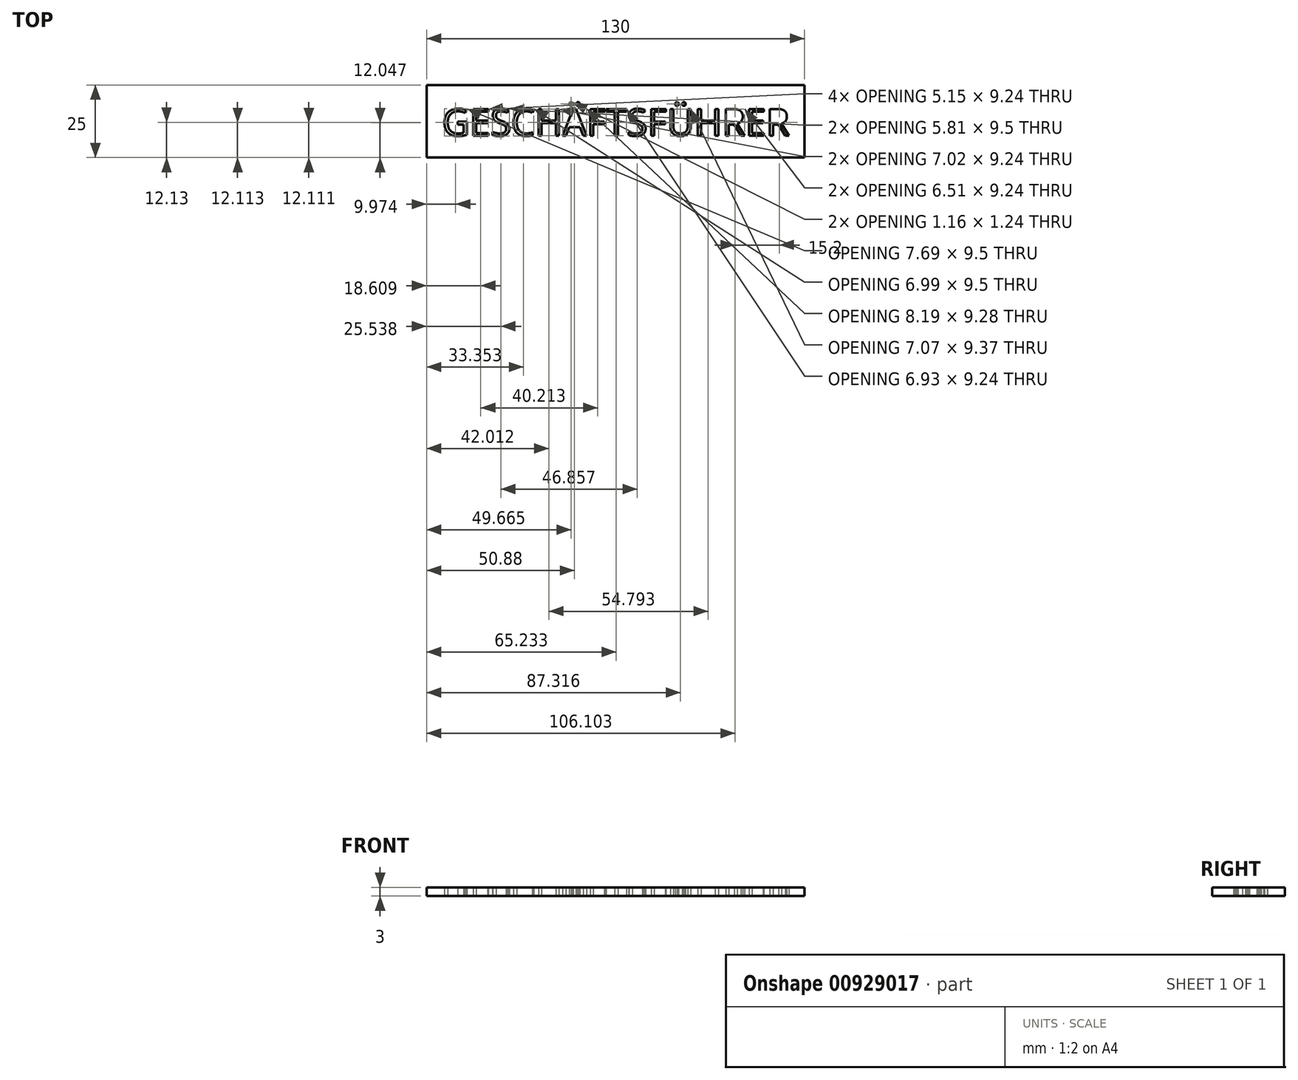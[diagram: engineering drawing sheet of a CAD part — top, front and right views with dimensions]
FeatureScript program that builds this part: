
annotation { "Feature Type Name" : "Feature", "Feature Type Description" : "" }
export const myFeature = defineFeature(function(context is Context, id is Id, definition is map)
    precondition{}
    {
        {
            var Q0;
            Q0=qCreatedBy(makeId("Top.planeOp"),FACE);
            var sketch = newSketch(context, id + "F0", { "sketchPlane" : qUnion([Q0])});
            skLineSegment(sketch, "E0.bottom", {"start": v(-88.08, 10.53) * mm, "end": v(41.92, 10.53) * mm});
            skLineSegment(sketch, "E0.top", {"start": v(-88.08, -14.47) * mm, "end": v(41.92, -14.47) * mm});
            skLineSegment(sketch, "E0.left", {"start": v(-88.08, 10.53) * mm, "end": v(-88.08, -14.47) * mm});
            skLineSegment(sketch, "E0.right", {"start": v(41.92, 10.53) * mm, "end": v(41.92, -14.47) * mm});
            skText(sketch, "E1", { "text": "GESCHÄFTSFÜHRER", "fontName": "OpenSans-Regular.ttf"});
            const initialGuessF0  = {"E1": [-0.08274, -0.00698, 1, 0, 0.00932]};
            skSetInitialGuess(sketch, initialGuessF0);
            skSolve(sketch);
        }
        {
            var Q0;
            Q0=makeQuery(id+"F0.imprint","IMPRINT",FACE,{"disambiguationData":[TD([[makeQuery(id+"F0.imprint","IMPRINT",EDGE,{"derivedFrom":sQuery(id+"F0.wireOp",EDGE,"E0.bottom")}),-1.0]])]});
            extrude(context, id + "F1", {"entities" : qUnion([Q0]), "depth" : 3 * mm, "offsetDistance" : 25 * mm});
        }
    });
